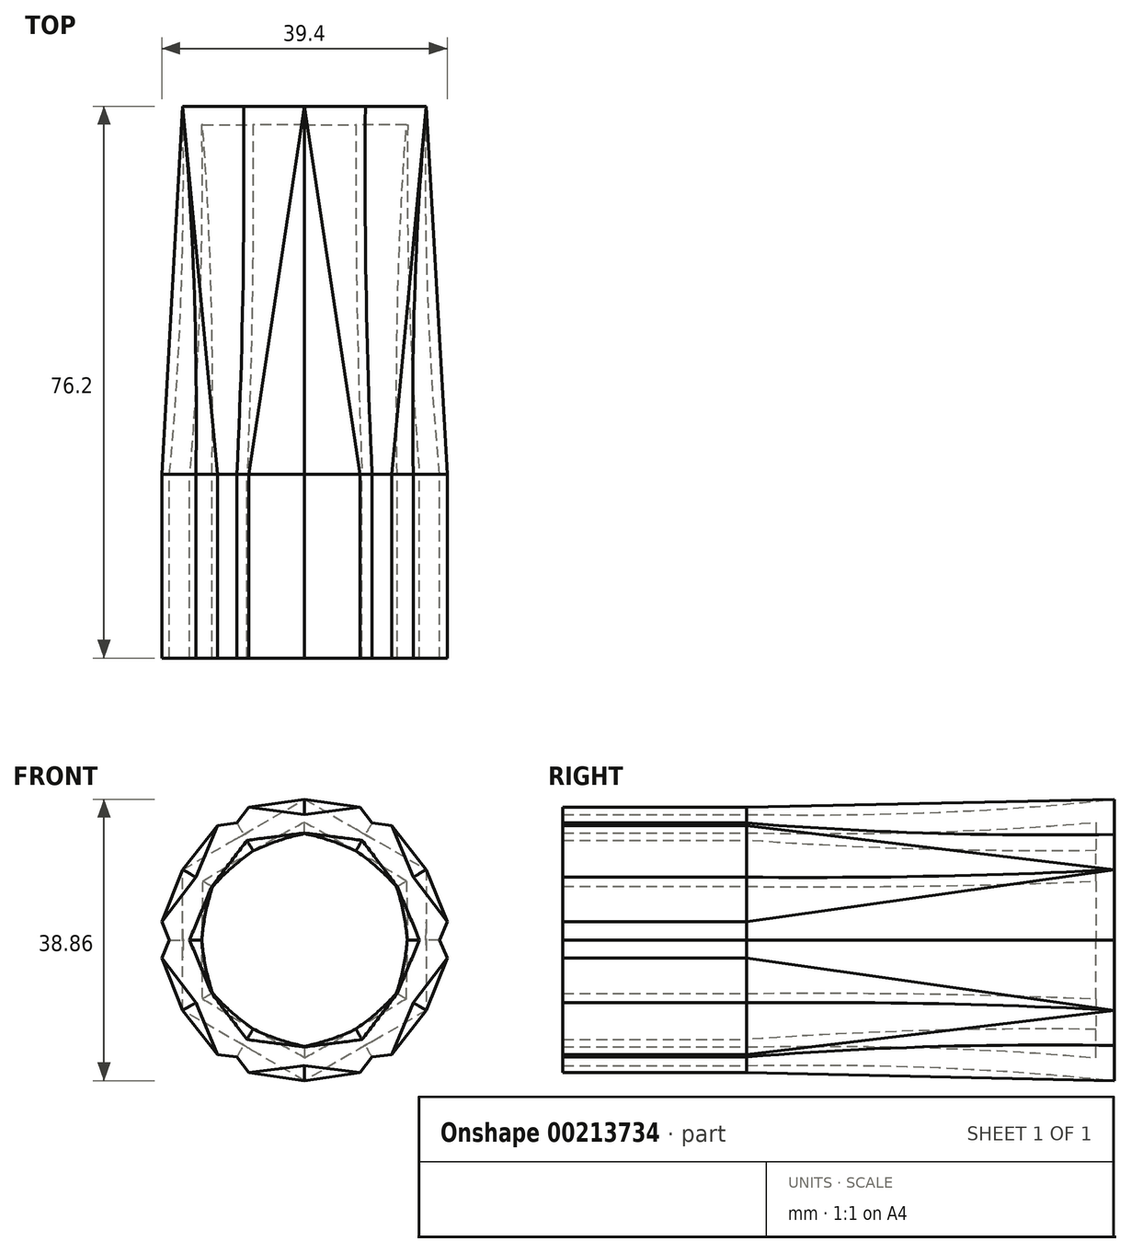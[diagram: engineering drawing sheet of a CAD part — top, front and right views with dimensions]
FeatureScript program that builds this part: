
annotation { "Feature Type Name" : "Feature", "Feature Type Description" : "" }
export const myFeature = defineFeature(function(context is Context, id is Id, definition is map)
    precondition{}
    {
        {
            var Q0;
            Q0=qCreatedBy(makeId("Front.planeOp"),FACE);
            cPlane(context, id + "F0", {"entities" : qUnion([Q0]), "cplaneType" : CPlaneType.OFFSET, "offset" : 50.8 * mm, "width" : 152.4 * mm, "height" : 152.4 * mm});
        }
        {
            var Q0;
            Q0=qCreatedBy(makeId("Front.planeOp"),FACE);
            var sketch = newSketch(context, id + "F1", { "sketchPlane" : qUnion([Q0])});
            skCircle(sketch, "E0.cCircle", {"center": v(0, 0) * mm, "radius": 16.83 * mm, "construction": true});
            skLineSegment(sketch, "E0.0", {"start": v(16.83, 9.72) * mm, "end": v(16.83, -9.72) * mm});
            skLineSegment(sketch, "E0.1", {"start": v(16.83, -9.72) * mm, "end": v(0, -19.43) * mm});
            skLineSegment(sketch, "E0.2", {"start": v(0, -19.43) * mm, "end": v(-16.83, -9.72) * mm});
            skLineSegment(sketch, "E0.3", {"start": v(-16.83, -9.72) * mm, "end": v(-16.83, 9.72) * mm});
            skLineSegment(sketch, "E0.4", {"start": v(-16.83, 9.72) * mm, "end": v(0, 19.43) * mm});
            skLineSegment(sketch, "E0.5", {"start": v(0, 19.43) * mm, "end": v(16.83, 9.72) * mm});
            skPoint(sketch, "E0.0.midPoint", {"position": v(16.83, 0) * mm});
            skSolve(sketch);
        }
        {
            var Q0;
            Q0=qCreatedBy(id+"F0.planeOp",FACE);
            var sketch = newSketch(context, id + "F2", { "sketchPlane" : qUnion([Q0])});
            skCircle(sketch, "E1.cCircle", {"center": v(0, 0) * mm, "radius": 17.2 * mm, "construction": true});
            skLineSegment(sketch, "E1.0", {"start": v(7.68, 18.32) * mm, "end": v(19.7, 2.5) * mm});
            skLineSegment(sketch, "E1.1", {"start": v(19.7, 2.5) * mm, "end": v(12.02, -15.8) * mm});
            skLineSegment(sketch, "E1.2", {"start": v(12.02, -15.8) * mm, "end": v(-7.68, -18.32) * mm});
            skLineSegment(sketch, "E1.3", {"start": v(-7.68, -18.32) * mm, "end": v(-19.7, -2.5) * mm});
            skLineSegment(sketch, "E1.4", {"start": v(-19.7, -2.5) * mm, "end": v(-12.02, 15.8) * mm});
            skLineSegment(sketch, "E1.5", {"start": v(-12.02, 15.8) * mm, "end": v(7.68, 18.32) * mm});
            skPoint(sketch, "E1.0.midPoint", {"position": v(13.7, 10.41) * mm});
            skSolve(sketch);
        }
        {
            var Q0;
            Q0=makeQuery(id+"F1.imprint","IMPRINT",FACE,{"disambiguationData":[TD([[makeQuery(id+"F1.imprint","IMPRINT",EDGE,{"derivedFrom":sQuery(id+"F1.wireOp",EDGE,"E0.0")}),-1.0]])]});
            var Q1;
            Q1=makeQuery(id+"F2.imprint","IMPRINT",FACE,{"disambiguationData":[TD([[makeQuery(id+"F2.imprint","IMPRINT",EDGE,{"derivedFrom":sQuery(id+"F2.wireOp",EDGE,"E1.0")}),-1.0]])]});
            loft(context, id + "F3", {"sheetProfilesArray" : [{ "sheetProfileEntities" : qUnion([Q0]) }, { "sheetProfileEntities" : qUnion([Q1]) }]});
        }
        {
            var Q0;
            Q0=makeQuery(id+"F3.opLoft","CAP_FACE",FACE,{"disambiguationData":[OSD([makeQuery(id+"F2.imprint","IMPRINT",FACE,{"disambiguationData":[TD([[makeQuery(id+"F2.imprint","IMPRINT",EDGE,{"derivedFrom":sQuery(id+"F2.wireOp",EDGE,"E1.0")}),-1.0]])]})])],"isStart":true});
            shell(context, id + "F4", {"entities" : qUnion([Q0]), "thickness" : 2.54 * mm});
        }
        {
            var Q0;
            Q0=makeQuery(id+"F3.opLoft","SWEPT_BODY",BODY,{"disambiguationData":[OSD([makeQuery(id+"F1.imprint","IMPRINT",FACE,{"disambiguationData":[TD([[makeQuery(id+"F1.imprint","IMPRINT",EDGE,{"derivedFrom":sQuery(id+"F1.wireOp",EDGE,"E0.0")}),-1.0]])]}),makeQuery(id+"F2.imprint","IMPRINT",FACE,{"disambiguationData":[TD([[makeQuery(id+"F2.imprint","IMPRINT",EDGE,{"derivedFrom":sQuery(id+"F2.wireOp",EDGE,"E1.0")}),-1.0]])]})])]});
            var Q1;
            Q1=qCreatedBy(makeId("Right.planeOp"),FACE);
            mirror(context, id + "F5", {"operationType" : NewBodyOperationType.ADD, "entities" : qUnion([Q0]), "mirrorPlane" : qUnion([Q1])});
        }
        {
            var Q0;
            {var subQ0=makeQuery(id+"F3.opLoft","CAP_FACE",FACE,{"disambiguationData":[OSD([makeQuery(id+"F2.imprint","IMPRINT",FACE,{"disambiguationData":[TD([[makeQuery(id+"F2.imprint","IMPRINT",EDGE,{"derivedFrom":sQuery(id+"F2.wireOp",EDGE,"E1.0")}),-1.0]])]})])],"isStart":true});Q0=makeQuery(id+"F5.boolean.opBoolean","MERGE",FACE,{"derivedFrom":[subQ0,makeQuery(id+"F5.opPattern","COPY",FACE,{"derivedFrom":subQ0,"instanceName":"1"})]});}
            extrude(context, id + "F6", {"entities" : qUnion([Q0]), "operationType" : NewBodyOperationType.ADD, "depth" : 25.4 * mm});
        }
    });
